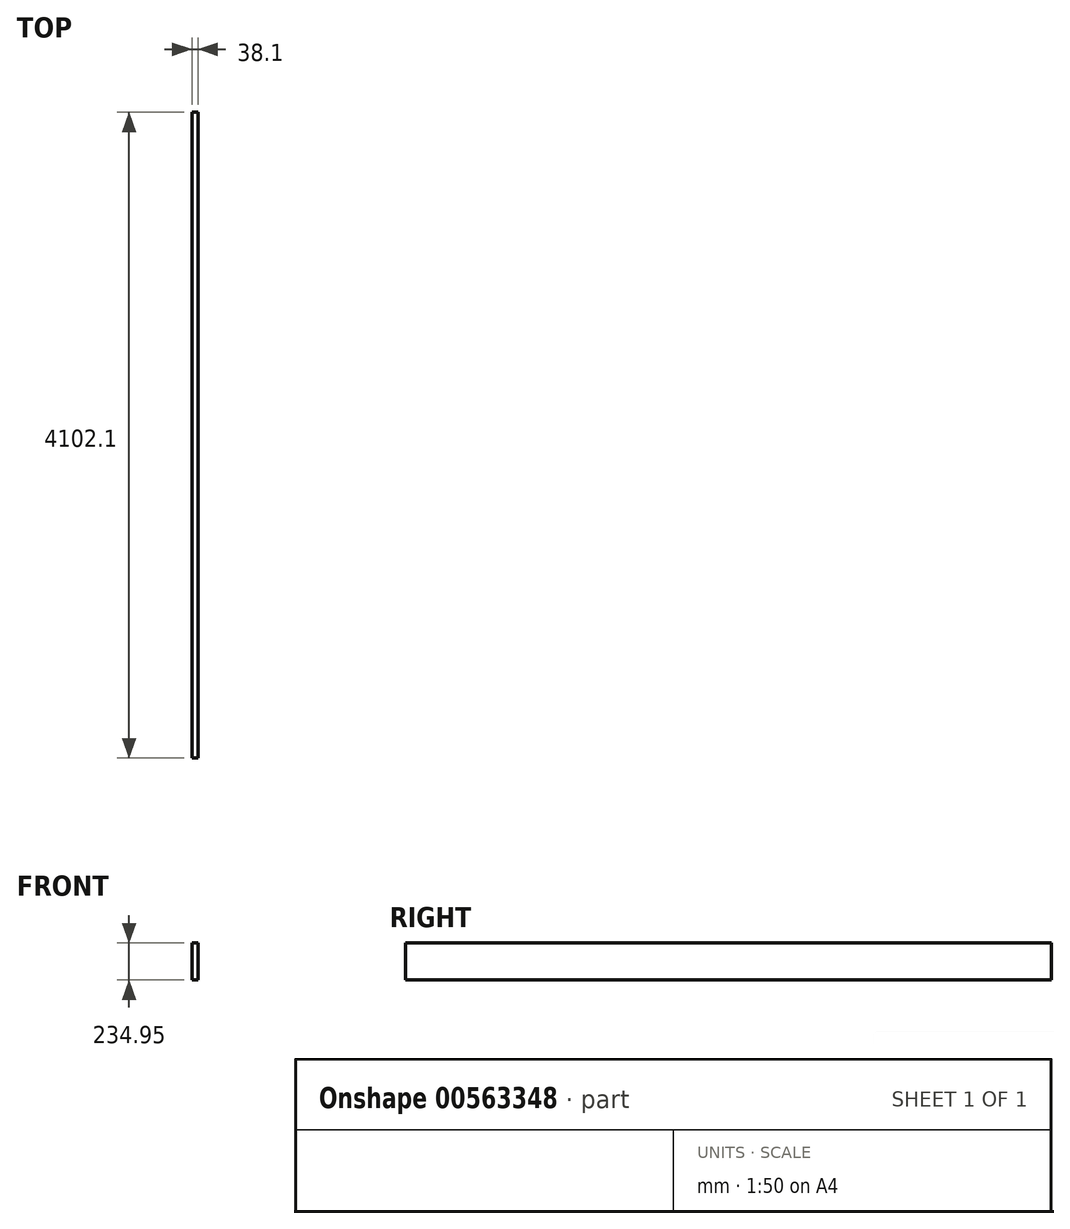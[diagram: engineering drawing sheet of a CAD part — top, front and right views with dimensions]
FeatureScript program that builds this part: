
annotation { "Feature Type Name" : "Feature", "Feature Type Description" : "" }
export const myFeature = defineFeature(function(context is Context, id is Id, definition is map)
    precondition{}
    {
        {
            var Q0;
            Q0=qCreatedBy(makeId("Top.planeOp"),FACE);
            var sketch = newSketch(context, id + "F0", { "sketchPlane" : qUnion([Q0])});
            skLineSegment(sketch, "E0.bottom", {"start": v(19.05, -2051.05) * mm, "end": v(-19.05, -2051.05) * mm});
            skLineSegment(sketch, "E0.top", {"start": v(19.05, 2051.05) * mm, "end": v(-19.05, 2051.05) * mm});
            skLineSegment(sketch, "E0.left", {"start": v(19.05, -2051.05) * mm, "end": v(19.05, 2051.05) * mm});
            skLineSegment(sketch, "E0.right", {"start": v(-19.05, -2051.05) * mm, "end": v(-19.05, 2051.05) * mm});
            skPoint(sketch, "E0.middle", {"position": v(0, 0) * mm});
            skSolve(sketch);
        }
        {
            var Q0;
            Q0 = qSketchRegion(id + "F0", true);
            extrude(context, id + "F1", {"entities" : qUnion([Q0]), "depth" : 234.95 * mm, "offsetDistance" : 25.4 * mm});
        }
    });
